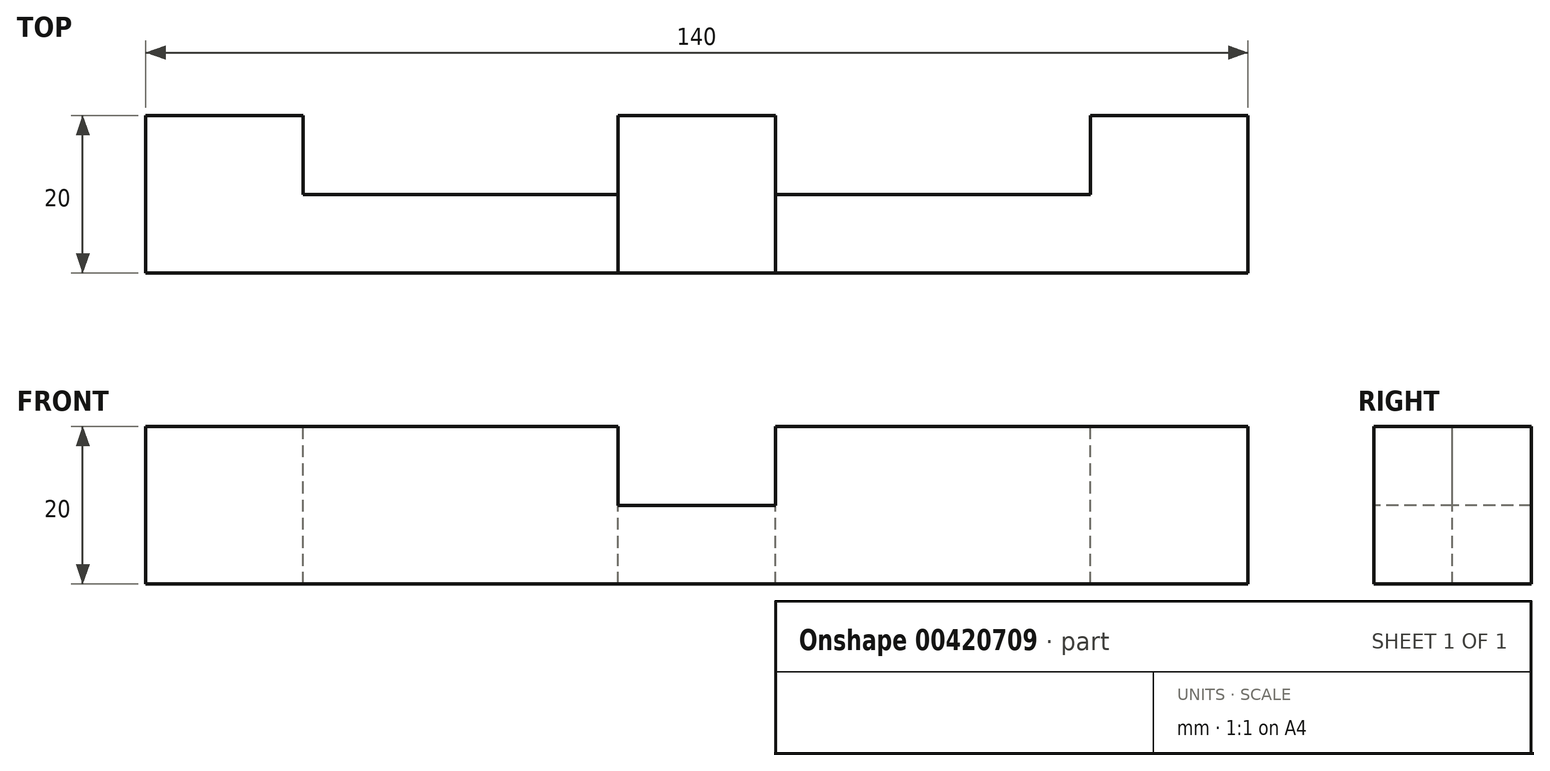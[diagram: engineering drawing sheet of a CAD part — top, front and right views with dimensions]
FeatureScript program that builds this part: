
annotation { "Feature Type Name" : "Feature", "Feature Type Description" : "" }
export const myFeature = defineFeature(function(context is Context, id is Id, definition is map)
    precondition{}
    {
        {
            var Q0;
            Q0=qCreatedBy(makeId("Right.planeOp"),FACE);
            var sketch = newSketch(context, id + "F0", { "sketchPlane" : qUnion([Q0])});
            skLineSegment(sketch, "E0.bottom", {"start": v(10, 10) * mm, "end": v(-10, 10) * mm});
            skLineSegment(sketch, "E0.top", {"start": v(10, -10) * mm, "end": v(-10, -10) * mm});
            skLineSegment(sketch, "E0.left", {"start": v(10, 10) * mm, "end": v(10, -10) * mm});
            skLineSegment(sketch, "E0.right", {"start": v(-10, 10) * mm, "end": v(-10, -10) * mm});
            skPoint(sketch, "E0.middle", {"position": v(0, 0) * mm});
            skSolve(sketch);
        }
        {
            var Q0;
            Q0=qSketchRegion(id+"F0",true);
            extrude(context, id + "F1", {"entities" : qUnion([Q0]), "endBound" : BoundingType.SYMMETRIC, "depth" : 140 * mm});
        }
        {
            var Q0;
            Q0=makeQuery(id+"F1.opExtrude","SWEPT_FACE",FACE,{"disambiguationData":[OSD([sQuery(id+"F0.wireOp",EDGE,"E0.right")])]});
            var sketch = newSketch(context, id + "F2", { "sketchPlane" : qUnion([Q0])});
            skLineSegment(sketch, "E1.bottom", {"start": v(-10, 10) * mm, "end": v(10, 10) * mm});
            skLineSegment(sketch, "E1.top", {"start": v(-10, 0) * mm, "end": v(10, 0) * mm});
            skLineSegment(sketch, "E1.left", {"start": v(-10, 10) * mm, "end": v(-10, 0) * mm});
            skLineSegment(sketch, "E1.right", {"start": v(10, 10) * mm, "end": v(10, 0) * mm});
            skSolve(sketch);
        }
        {
            var Q0;
            Q0=qSketchRegion(id+"F2",true);
            extrude(context, id + "F3", {"entities" : qUnion([Q0]), "operationType" : NewBodyOperationType.REMOVE, "oppositeDirection" : true, "depth" : 20 * mm});
        }
        {
            var Q0;
            {var subQ2=sQuery(id+"F0.wireOp",EDGE,"E0.bottom");Q0=makeQuery(id+"F3.boolean.opBoolean","SPLIT",FACE,{"disambiguationData":[TD([makeQuery(id+"F3.opExtrude","SWEPT_FACE",FACE,{"disambiguationData":[OSD([sQuery(id+"F2.wireOp",EDGE,"E1.right")])]})])],"derivedFrom":makeQuery(id+"F1.opExtrude","SWEPT_FACE",FACE,{"disambiguationData":[OSD([subQ2])]})});}
            var sketch = newSketch(context, id + "F4", { "sketchPlane" : qUnion([Q0])});
            skLineSegment(sketch, "E2.bottom", {"start": v(10, 10) * mm, "end": v(50, 10) * mm});
            skLineSegment(sketch, "E2.top", {"start": v(10, 0) * mm, "end": v(50, 0) * mm});
            skLineSegment(sketch, "E2.left", {"start": v(10, 10) * mm, "end": v(10, 0) * mm});
            skLineSegment(sketch, "E2.right", {"start": v(50, 10) * mm, "end": v(50, 0) * mm});
            skLineSegment(sketch, "E3.bottom", {"start": v(-10, 10) * mm, "end": v(-50, 10) * mm});
            skLineSegment(sketch, "E3.top", {"start": v(-10, 0) * mm, "end": v(-50, 0) * mm});
            skLineSegment(sketch, "E3.left", {"start": v(-10, 10) * mm, "end": v(-10, 0) * mm});
            skLineSegment(sketch, "E3.right", {"start": v(-50, 10) * mm, "end": v(-50, 0) * mm});
            skSolve(sketch);
        }
        {
            var Q0;
            Q0=qSketchRegion(id+"F4",true);
            extrude(context, id + "F5", {"entities" : qUnion([Q0]), "operationType" : NewBodyOperationType.REMOVE, "oppositeDirection" : true, "depth" : 20 * mm});
        }
    });
